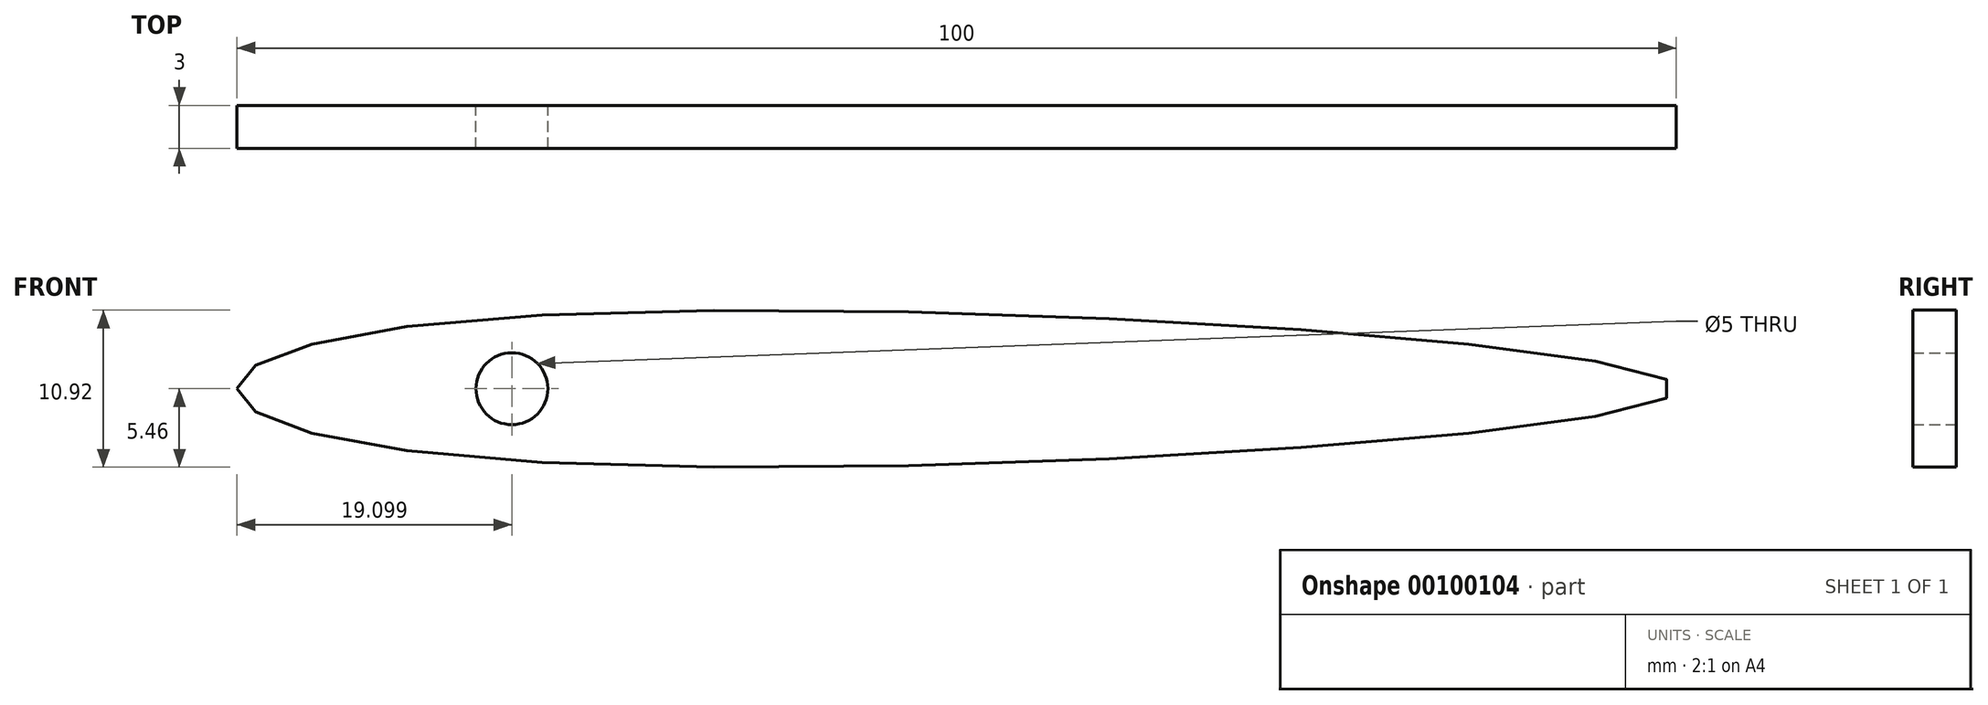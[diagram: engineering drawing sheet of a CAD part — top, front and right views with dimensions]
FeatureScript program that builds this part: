
annotation { "Feature Type Name" : "Feature", "Feature Type Description" : "" }
export const myFeature = defineFeature(function(context is Context, id is Id, definition is map)
    precondition{}
    {
        {
            var Q0;
            Q0=qCreatedBy(makeId("Front.planeOp"),FACE);
            var sketch = newSketch(context, id + "F0", { "sketchPlane" : qUnion([Q0])});
            skPoint(sketch, "E0", {"position": v(100, 0) * mm});
            skPoint(sketch, "E1", {"position": v(19.1, 0) * mm});
            skPoint(sketch, "E2", {"position": v(19.1, 5) * mm});
            skPoint(sketch, "E3", {"position": v(19.1, -5) * mm});
            skFitSpline(sketch, "E4", {"points": [v(0, 0) * mm, v(19.1, 5) * mm, v(100, 0) * mm, v(19.1, -5) * mm, v(0, 0) * mm]});
            skCircle(sketch, "E5", {"center": v(19.1, 0) * mm, "radius": 2.5 * mm});
            skSolve(sketch);
        }
        {
            var Q0;
            Q0=makeQuery(id+"F0.imprint","IMPRINT",FACE,{"disambiguationData":[TD([[makeQuery(id+"F0.imprint","IMPRINT",EDGE,{"derivedFrom":sQuery(id+"F0.wireOp",EDGE,"E4")}),-1.0]])]});
            extrude(context, id + "F1", {"entities" : qUnion([Q0]), "depth" : 3 * mm});
        }
    });
